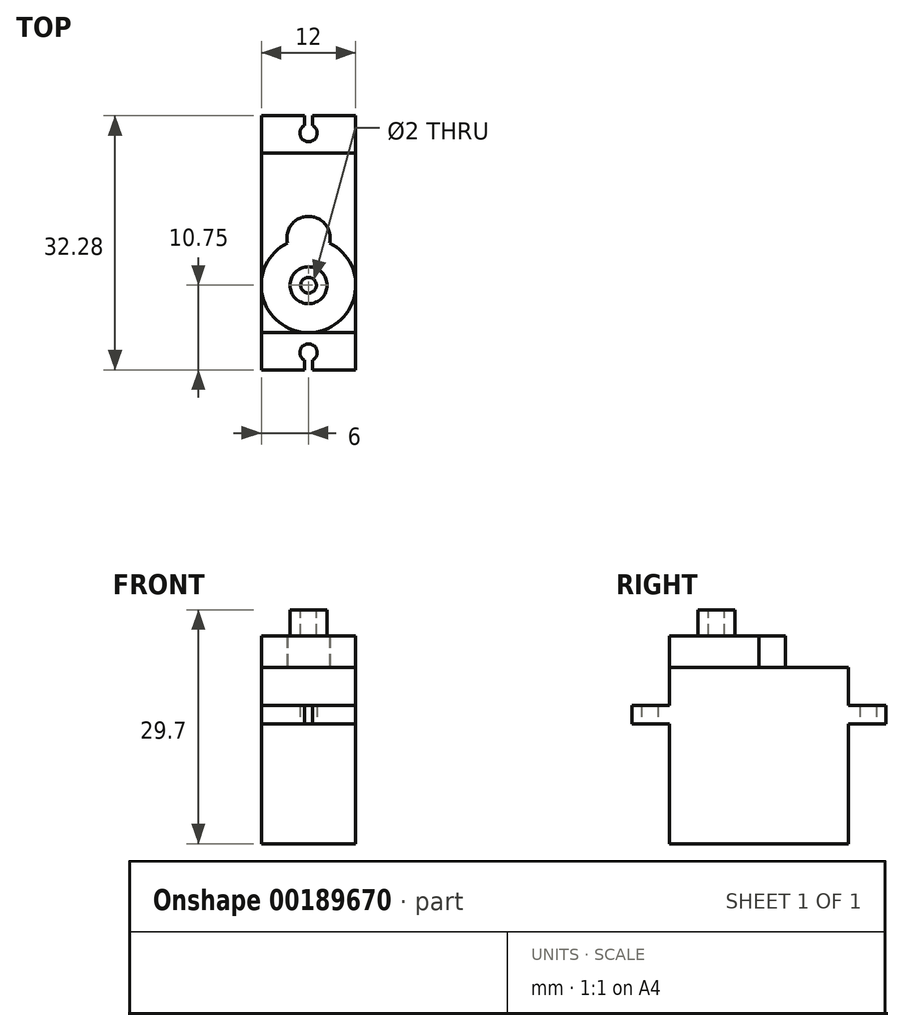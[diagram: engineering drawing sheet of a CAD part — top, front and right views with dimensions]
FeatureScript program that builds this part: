
annotation { "Feature Type Name" : "Feature", "Feature Type Description" : "" }
export const myFeature = defineFeature(function(context is Context, id is Id, definition is map)
    precondition{}
    {
        {
            var Q0;
            Q0=qCreatedBy(makeId("Top.planeOp"),FACE);
            var sketch = newSketch(context, id + "F0", { "sketchPlane" : qUnion([Q0])});
            skLineSegment(sketch, "E0.bottom", {"start": v(6, 11.4) * mm, "end": v(-6, 11.4) * mm});
            skLineSegment(sketch, "E0.top", {"start": v(6, -11.39) * mm, "end": v(-6, -11.39) * mm});
            skLineSegment(sketch, "E0.left", {"start": v(6, 11.4) * mm, "end": v(6, -11.39) * mm});
            skLineSegment(sketch, "E0.right", {"start": v(-6, 11.4) * mm, "end": v(-6, -11.39) * mm});
            skPoint(sketch, "E0.middle", {"position": v(0, 0) * mm});
            skSolve(sketch);
        }
        {
            var Q0;
            Q0=makeQuery(id+"F0.imprint","IMPRINT",FACE,{"disambiguationData":[TD([[makeQuery(id+"F0.imprint","IMPRINT",EDGE,{"derivedFrom":sQuery(id+"F0.wireOp",EDGE,"E0.bottom")}),1.0]])]});
            extrude(context, id + "F1", {"entities" : qUnion([Q0]), "depth" : 15.2 * mm});
        }
        {
            var Q0;
            Q0=makeQuery(id+"F1.opExtrude","CAP_FACE",FACE,{"disambiguationData":[OSD([sQuery(id+"F0.wireOp",EDGE,"E0.bottom"),sQuery(id+"F0.wireOp",EDGE,"E0.top"),sQuery(id+"F0.wireOp",EDGE,"E0.left"),sQuery(id+"F0.wireOp",EDGE,"E0.right")])],"isStart":false});
            var sketch = newSketch(context, id + "F2", { "sketchPlane" : qUnion([Q0])});
            skLineSegment(sketch, "E1.0", {"start": v(-6, 11.4) * mm, "end": v(-6, -11.39) * mm});
            skLineSegment(sketch, "E2.0", {"start": v(6, 11.4) * mm, "end": v(6, -11.39) * mm});
            skLineSegment(sketch, "E3", {"start": v(-6, 11.4) * mm, "end": v(-6, 16.14) * mm});
            skLineSegment(sketch, "E4", {"start": v(-6, 16.14) * mm, "end": v(-0.5, 16.14) * mm});
            skLineSegment(sketch, "E5", {"start": v(6, 16.14) * mm, "end": v(6, 11.4) * mm});
            skLineSegment(sketch, "E6", {"start": v(0, 0) * mm, "end": v(-2.1, 0) * mm, "construction": true});
            skLineSegment(sketch, "E7", {"start": v(0, 16.14) * mm, "end": v(0, 13.94) * mm, "construction": true});
            skPoint(sketch, "E7.endSnap0", {"position": v(0, 16.14) * mm});
            skArc(sketch, "E8", {"start": v(-0.5, 14.92) * mm, "mid": v(0, 12.84) * mm, "end": v(0.5, 14.92) * mm});
            skLineSegment(sketch, "E9", {"start": v(0.5, 14.92) * mm, "end": v(0.5, 16.14) * mm});
            skLineSegment(sketch, "E10.MirrorCS", {"start": v(-0.5, 14.92) * mm, "end": v(-0.5, 16.14) * mm});
            skLineSegment(sketch, "E11.MirrorCS", {"start": v(-6, -11.4) * mm, "end": v(-6, -16.14) * mm});
            skLineSegment(sketch, "E12.MirrorCS", {"start": v(-6, -16.14) * mm, "end": v(-0.5, -16.14) * mm});
            skLineSegment(sketch, "E13.MirrorCS", {"start": v(-0.5, -14.92) * mm, "end": v(-0.5, -16.14) * mm});
            skArc(sketch, "E14.MirrorCS", {"start": v(-0.5, -14.92) * mm, "mid": v(0, -12.84) * mm, "end": v(0.5, -14.92) * mm});
            skLineSegment(sketch, "E15.MirrorCS", {"start": v(0.5, -14.92) * mm, "end": v(0.5, -16.14) * mm});
            skLineSegment(sketch, "E16.MirrorCS", {"start": v(6, -16.14) * mm, "end": v(6, -11.4) * mm});
            skLineSegment(sketch, "E17.trimOffspring", {"start": v(0.5, 16.14) * mm, "end": v(6, 16.14) * mm});
            skLineSegment(sketch, "E18.trimOffspring", {"start": v(0.5, -16.14) * mm, "end": v(6, -16.14) * mm});
            skSolve(sketch);
        }
        {
            var Q0;
            Q0=makeQuery(id+"F2.imprint","IMPRINT",FACE,{"disambiguationData":[TD([[makeQuery(id+"F2.imprint","IMPRINT",EDGE,{"derivedFrom":sQuery(id+"F2.wireOp",EDGE,"E3")}),-1.0]])]});
            var Q1;
            Q1=makeQuery(id+"F2.imprint","IMPRINT",FACE,{"disambiguationData":[TD([[makeQuery(id+"F2.imprint","IMPRINT",EDGE,{"derivedFrom":sQuery(id+"F2.wireOp",EDGE,"E1.0")}),1.0]])]});
            var Q2;
            Q2=makeQuery(id+"F2.imprint","IMPRINT",FACE,{"disambiguationData":[TD([[makeQuery(id+"F2.imprint","IMPRINT",EDGE,{"derivedFrom":sQuery(id+"F2.wireOp",EDGE,"E11.MirrorCS")}),1.0]])]});
            extrude(context, id + "F3", {"entities" : qUnion([Q0, Q1, Q2]), "operationType" : NewBodyOperationType.ADD, "depth" : 2.4 * mm});
        }
        {
            var Q0;
            Q0=makeQuery(id+"F3.opExtrude","CAP_FACE",FACE,{"disambiguationData":[OSD([sQuery(id+"F2.wireOp",EDGE,"E1.0"),sQuery(id+"F2.wireOp",EDGE,"E2.0"),sQuery(id+"F2.wireOp",EDGE,"E3"),sQuery(id+"F2.wireOp",EDGE,"E4"),sQuery(id+"F2.wireOp",EDGE,"E5"),sQuery(id+"F2.wireOp",EDGE,"E8"),sQuery(id+"F2.wireOp",EDGE,"E9"),sQuery(id+"F2.wireOp",EDGE,"E10.MirrorCS"),sQuery(id+"F2.wireOp",EDGE,"E11.MirrorCS"),sQuery(id+"F2.wireOp",EDGE,"E13.MirrorCS"),sQuery(id+"F2.wireOp",EDGE,"E14.MirrorCS"),sQuery(id+"F2.wireOp",EDGE,"E15.MirrorCS"),sQuery(id+"F2.wireOp",EDGE,"E12.MirrorCS"),sQuery(id+"F2.wireOp",EDGE,"E16.MirrorCS"),sQuery(id+"F2.wireOp",EDGE,"E17.trimOffspring"),sQuery(id+"F2.wireOp",EDGE,"E18.trimOffspring")])],"isStart":false});
            var sketch = newSketch(context, id + "F4", { "sketchPlane" : qUnion([Q0])});
            skLineSegment(sketch, "E19.0", {"start": v(6, -11.39) * mm, "end": v(-6, -11.39) * mm});
            skLineSegment(sketch, "E20.0", {"start": v(6, 11.4) * mm, "end": v(-6, 11.4) * mm});
            skLineSegment(sketch, "E21", {"start": v(6, 11.4) * mm, "end": v(6, -11.39) * mm});
            skLineSegment(sketch, "E22", {"start": v(-6, 11.4) * mm, "end": v(-6, -11.39) * mm});
            skSolve(sketch);
        }
        {
            var Q0;
            Q0=makeQuery(id+"F4.imprint","IMPRINT",FACE,{"disambiguationData":[TD([[makeQuery(id+"F4.imprint","IMPRINT",EDGE,{"derivedFrom":sQuery(id+"F4.wireOp",EDGE,"E19.0")}),-1.0]])]});
            extrude(context, id + "F5", {"entities" : qUnion([Q0]), "operationType" : NewBodyOperationType.ADD, "depth" : 4.8 * mm});
        }
        {
            var Q0;
            Q0=makeQuery(id+"F5.opExtrude","CAP_FACE",FACE,{"disambiguationData":[OSD([sQuery(id+"F4.wireOp",EDGE,"E19.0"),sQuery(id+"F4.wireOp",EDGE,"E20.0"),sQuery(id+"F4.wireOp",EDGE,"E21"),sQuery(id+"F4.wireOp",EDGE,"E22")])],"isStart":false});
            var sketch = newSketch(context, id + "F6", { "sketchPlane" : qUnion([Q0])});
            skCircle(sketch, "E23", {"center": v(0, -5.39) * mm, "radius": 6 * mm});
            skLineSegment(sketch, "E24.0", {"start": v(6, -11.39) * mm, "end": v(-6, -11.39) * mm, "construction": true});
            skCircle(sketch, "E25", {"center": v(0, 0.61) * mm, "radius": 2.75 * mm});
            skSolve(sketch);
        }
        {
            var Q0;
            Q0 = qSketchRegion(id + "F6", true);
            extrude(context, id + "F7", {"entities" : qUnion([Q0]), "operationType" : NewBodyOperationType.ADD, "depth" : 4 * mm});
        }
        {
            var Q0;
            Q0=makeQuery(id+"F7.opExtrude","CAP_FACE",FACE,{"disambiguationData":[OSD([sQuery(id+"F6.wireOp",EDGE,"E23"),sQuery(id+"F6.wireOp",EDGE,"E25")])],"isStart":false});
            var sketch = newSketch(context, id + "F8", { "sketchPlane" : qUnion([Q0])});
            skCircle(sketch, "E26", {"center": v(0, -5.39) * mm, "radius": 2.35 * mm});
            skSolve(sketch);
        }
        {
            var Q0;
            Q0=makeQuery(id+"F8.imprint","IMPRINT",FACE,{"disambiguationData":[TD([[makeQuery(id+"F8.imprint","IMPRINT",EDGE,{"derivedFrom":sQuery(id+"F8.wireOp",EDGE,"E26")}),1.0]])]});
            extrude(context, id + "F9", {"entities" : qUnion([Q0]), "depth" : 3.3 * mm});
        }
        {
            var Q0;
            Q0=makeQuery(id+"F9.opExtrude","CAP_FACE",FACE,{"disambiguationData":[OSD([sQuery(id+"F8.wireOp",EDGE,"E26")])],"isStart":false});
            var sketch = newSketch(context, id + "F10", { "sketchPlane" : qUnion([Q0])});
            skCircle(sketch, "E27", {"center": v(0, -5.39) * mm, "radius": 1 * mm});
            skSolve(sketch);
        }
        {
            var Q0;
            Q0=makeQuery(id+"F10.imprint","IMPRINT",FACE,{"disambiguationData":[TD([[makeQuery(id+"F10.imprint","IMPRINT",EDGE,{"derivedFrom":sQuery(id+"F10.wireOp",EDGE,"E27")}),1.0]])]});
            var Q1;
            Q1=makeQuery(id+"F9.opExtrude","CAP_FACE",FACE,{"disambiguationData":[OSD([sQuery(id+"F8.wireOp",EDGE,"E26")])],"isStart":true});
            extrude(context, id + "F11", {"entities" : qUnion([Q0]), "operationType" : NewBodyOperationType.REMOVE, "endBound" : BoundingType.UP_TO_SURFACE, "oppositeDirection" : true, "endBoundEntityFace" : qUnion([Q1]), "depth" : 25 * mm});
        }
    });
